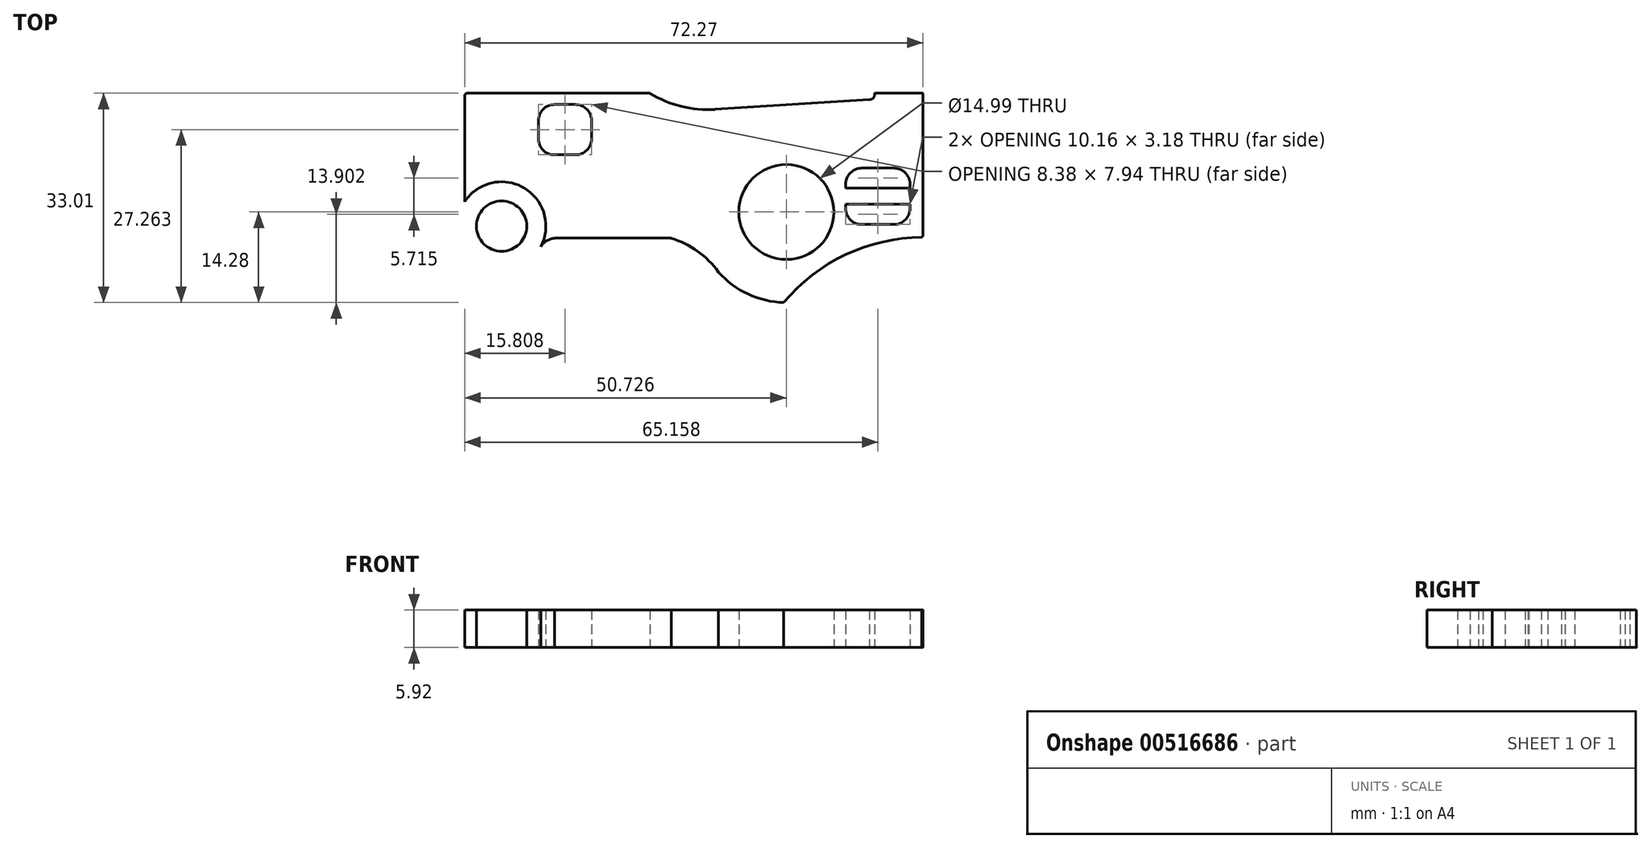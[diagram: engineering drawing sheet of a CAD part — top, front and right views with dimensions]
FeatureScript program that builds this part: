
annotation { "Feature Type Name" : "Feature", "Feature Type Description" : "" }
export const myFeature = defineFeature(function(context is Context, id is Id, definition is map)
    precondition{}
    {
        {
            var Q0;
            Q0=qCreatedBy(makeId("Top.planeOp"),FACE);
            var sketch = newSketch(context, id + "F0", { "sketchPlane" : qUnion([Q0])});
            skLineSegment(sketch, "E0.bottom", {"start": v(39.25, -10.6) * mm, "end": v(31.72, -10.6) * mm});
            skLineSegment(sketch, "E1.trimOffspring", {"start": v(-3.76, -10.6) * mm, "end": v(-32.6, -10.6) * mm});
            skLineSegment(sketch, "E2.MirrorCS", {"start": v(31.67, -10.8) * mm, "end": v(31.67, -10.64) * mm});
            skArc(sketch, "E3.MirrorCS", {"start": v(31.67, -10.8) * mm, "mid": v(31.43, -11.37) * mm, "end": v(30.86, -11.6) * mm});
            skArc(sketch, "E4.MirrorCS", {"start": v(31.67, -10.64) * mm, "mid": v(31.69, -10.6) * mm, "end": v(31.72, -10.6) * mm});
            skArc(sketch, "E5.MirrorCS", {"start": v(39.25, -10.6) * mm, "mid": v(39.29, -10.6) * mm, "end": v(39.3, -10.64) * mm});
            skLineSegment(sketch, "E6.MirrorCS", {"start": v(-29.64, -12.5) * mm, "end": v(-29.8, -12.5) * mm});
            skLineSegment(sketch, "E7.MirrorCS", {"start": v(-27.09, -21.38) * mm, "end": v(-27.1, -21.38) * mm});
            skArc(sketch, "E8.MirrorCS", {"start": v(-32.97, -10.97) * mm, "mid": v(-32.86, -10.7) * mm, "end": v(-32.6, -10.6) * mm});
            skArc(sketch, "E9.MirrorCS", {"start": v(-31.06, -13.76) * mm, "mid": v(-30.7, -12.87) * mm, "end": v(-29.8, -12.5) * mm});
            skArc(sketch, "E10.MirrorCS", {"start": v(-25.82, -13.76) * mm, "mid": v(-25.45, -12.87) * mm, "end": v(-24.55, -12.5) * mm});
            skArc(sketch, "E11.MirrorCS", {"start": v(-24.4, -12.5) * mm, "mid": v(-23.5, -12.87) * mm, "end": v(-23.13, -13.76) * mm});
            skArc(sketch, "E12.MirrorCS", {"start": v(-27.1, -21.38) * mm, "mid": v(-28, -21.01) * mm, "end": v(-28.37, -20.11) * mm});
            skArc(sketch, "E13.MirrorCS", {"start": v(-25.82, -20.11) * mm, "mid": v(-26.19, -21.01) * mm, "end": v(-27.09, -21.38) * mm});
            skArc(sketch, "E14.MirrorCS", {"start": v(-29.64, -12.5) * mm, "mid": v(-28.74, -12.87) * mm, "end": v(-28.37, -13.76) * mm});
            skLineSegment(sketch, "E15.MirrorCS", {"start": v(-24.55, -12.5) * mm, "end": v(-24.4, -12.5) * mm});
            skLineSegment(sketch, "E16.MirrorCS", {"start": v(-21.35, -25.87) * mm, "end": v(-21.35, -27.66) * mm});
            skArc(sketch, "E17.MirrorCS", {"start": v(39.3, -32.94) * mm, "mid": v(39.26, -33.15) * mm, "end": v(39.13, -33.32) * mm});
            skLineSegment(sketch, "E18.MirrorCS", {"start": v(4.8, -17.77) * mm, "end": v(4.8, -17.33) * mm});
            skLineSegment(sketch, "E19.MirrorCS", {"start": v(-1.92, -13.96) * mm, "end": v(2.73, -14.84) * mm});
            skArc(sketch, "E20.MirrorCS", {"start": v(-18.81, -20.3) * mm, "mid": v(-20.6, -19.56) * mm, "end": v(-21.35, -17.77) * mm});
            skLineSegment(sketch, "E21.MirrorCS", {"start": v(37.27, -28.75) * mm, "end": v(37.27, -24.94) * mm});
            skArc(sketch, "E22.MirrorCS", {"start": v(-21.35, -25.87) * mm, "mid": v(-20.6, -24.08) * mm, "end": v(-18.81, -23.33) * mm});
            skArc(sketch, "E23.MirrorCS", {"start": v(4.8, -17.77) * mm, "mid": v(4.06, -19.56) * mm, "end": v(2.26, -20.3) * mm});
            skArc(sketch, "E24.MirrorCS", {"start": v(-12.97, -17.77) * mm, "mid": v(-13.72, -19.56) * mm, "end": v(-15.51, -20.3) * mm});
            skArc(sketch, "E25.MirrorCS", {"start": v(29.65, -31.29) * mm, "mid": v(27.85, -30.54) * mm, "end": v(27.1, -28.75) * mm});
            skArc(sketch, "E26.MirrorCS", {"start": v(-18.81, -31.55) * mm, "mid": v(-19.53, -31.44) * mm, "end": v(-20.18, -31.15) * mm});
            skArc(sketch, "E27.MirrorCS", {"start": v(-21.35, -14.9) * mm, "mid": v(-20.6, -13.11) * mm, "end": v(-18.81, -12.37) * mm});
            skArc(sketch, "E28.MirrorCS", {"start": v(2.73, -14.84) * mm, "mid": v(4.22, -15.71) * mm, "end": v(4.8, -17.33) * mm});
            skArc(sketch, "E29.MirrorCS", {"start": v(-15.51, -12.37) * mm, "mid": v(-13.72, -13.11) * mm, "end": v(-12.97, -14.9) * mm});
            skArc(sketch, "E30.MirrorCS", {"start": v(27.1, -24.94) * mm, "mid": v(27.85, -23.14) * mm, "end": v(29.65, -22.4) * mm});
            skLineSegment(sketch, "E31.MirrorCS", {"start": v(-1.92, -20.3) * mm, "end": v(2.26, -20.3) * mm});
            skArc(sketch, "E32.MirrorCS", {"start": v(34.73, -22.4) * mm, "mid": v(36.52, -23.14) * mm, "end": v(37.27, -24.94) * mm});
            skLineSegment(sketch, "E33.MirrorCS", {"start": v(-4.46, -17.77) * mm, "end": v(-4.46, -16.5) * mm});
            skLineSegment(sketch, "E34.MirrorCS", {"start": v(-21.35, -17.77) * mm, "end": v(-21.35, -14.9) * mm});
            skLineSegment(sketch, "E35.MirrorCS", {"start": v(6.1, -13.27) * mm, "end": v(6.1, -20.26) * mm});
            skArc(sketch, "E36.MirrorCS", {"start": v(-1.92, -20.3) * mm, "mid": v(-3.72, -19.56) * mm, "end": v(-4.46, -17.77) * mm});
            skLineSegment(sketch, "E37.MirrorCS", {"start": v(-12.97, -17.77) * mm, "end": v(-12.97, -14.9) * mm});
            skArc(sketch, "E38.MirrorCS", {"start": v(37.27, -28.75) * mm, "mid": v(36.52, -30.54) * mm, "end": v(34.73, -31.29) * mm});
            skLineSegment(sketch, "E39.MirrorCS", {"start": v(4.73, -30.07) * mm, "end": v(6.18, -26.94) * mm});
            skArc(sketch, "E40.MirrorCS", {"start": v(-4.46, -16.5) * mm, "mid": v(-3.72, -14.7) * mm, "end": v(-1.92, -13.96) * mm});
            skLineSegment(sketch, "E41.MirrorCS", {"start": v(-18.81, -20.3) * mm, "end": v(-15.51, -20.3) * mm});
            skLineSegment(sketch, "E42.MirrorCS", {"start": v(-18.81, -12.37) * mm, "end": v(-15.51, -12.37) * mm});
            skLineSegment(sketch, "E43.MirrorCS", {"start": v(27.1, -28.75) * mm, "end": v(27.1, -24.94) * mm});
            skArc(sketch, "E44.MirrorCS", {"start": v(4.73, -30.07) * mm, "mid": v(3.8, -31.15) * mm, "end": v(2.43, -31.55) * mm});
            skArc(sketch, "E45.MirrorCS", {"start": v(-21.07, -34.98) * mm, "mid": v(-20.15, -33.92) * mm, "end": v(-18.83, -33.45) * mm});
            skPoint(sketch, "E46.MirrorP", {"position": v(2.6, -27.6) * mm});
            skLineSegment(sketch, "E47.MirrorCS", {"start": v(-23.13, -25.84) * mm, "end": v(-23.13, -13.76) * mm});
            skLineSegment(sketch, "E48.MirrorCS", {"start": v(-31.06, -13.76) * mm, "end": v(-31.06, -25.76) * mm});
            skCircle(sketch, "E49.MirrorC", {"center": v(17.76, -29.32) * mm, "radius": 7.5 * mm});
            skLineSegment(sketch, "E50.MirrorCS", {"start": v(-25.82, -20.11) * mm, "end": v(-25.82, -13.76) * mm});
            skLineSegment(sketch, "E51.MirrorCS", {"start": v(-32.97, -10.97) * mm, "end": v(-32.97, -27.68) * mm});
            skArc(sketch, "E52.MirrorCS", {"start": v(17.35, -43.6) * mm, "mid": v(11.71, -42.27) * mm, "end": v(7.07, -38.8) * mm});
            skLineSegment(sketch, "E53.MirrorCS", {"start": v(-18.81, -31.55) * mm, "end": v(2.43, -31.55) * mm});
            skLineSegment(sketch, "E54.MirrorCS", {"start": v(-28.37, -20.11) * mm, "end": v(-28.37, -13.76) * mm});
            skArc(sketch, "E55.MirrorCS", {"start": v(17.35, -43.6) * mm, "mid": v(27.1, -36.05) * mm, "end": v(39.13, -33.32) * mm});
            skLineSegment(sketch, "E56.MirrorCS", {"start": v(-0.42, -33.45) * mm, "end": v(-18.83, -33.45) * mm});
            skLineSegment(sketch, "E57.MirrorCS", {"start": v(-18.81, -23.33) * mm, "end": v(3.88, -23.33) * mm});
            skLineSegment(sketch, "E58.MirrorCS", {"start": v(30.88, -11.73) * mm, "end": v(30.88, -18.71) * mm});
            skLineSegment(sketch, "E59.MirrorCS", {"start": v(6.1, -20.26) * mm, "end": v(30.88, -18.71) * mm});
            skLineSegment(sketch, "E60.MirrorCS", {"start": v(39.3, -32.94) * mm, "end": v(39.3, -10.64) * mm});
            skLineSegment(sketch, "E61.MirrorCS", {"start": v(30.86, -11.6) * mm, "end": v(6.53, -13.13) * mm});
            skArc(sketch, "E62.MirrorCS", {"start": v(6.53, -13.13) * mm, "mid": v(1.19, -12.65) * mm, "end": v(-3.76, -10.6) * mm});
            skCircle(sketch, "E63.MirrorC", {"center": v(17.76, -29.32) * mm, "radius": 6.03 * mm});
            skLineSegment(sketch, "E64.MirrorCS", {"start": v(6.1, -13.27) * mm, "end": v(30.88, -11.73) * mm});
            skLineSegment(sketch, "E65.MirrorCS", {"start": v(34.73, -31.29) * mm, "end": v(29.65, -31.29) * mm});
            skArc(sketch, "E66.MirrorCS", {"start": v(-0.42, -33.45) * mm, "mid": v(3.77, -35.52) * mm, "end": v(7.07, -38.8) * mm});
            skLineSegment(sketch, "E67.MirrorCS", {"start": v(27.1, -28.11) * mm, "end": v(37.27, -28.11) * mm});
            skArc(sketch, "E68.MirrorCS", {"start": v(-31.06, -25.76) * mm, "mid": v(-27.08, -24.56) * mm, "end": v(-23.13, -25.84) * mm});
            skLineSegment(sketch, "E69.MirrorCS", {"start": v(34.73, -22.4) * mm, "end": v(29.65, -22.4) * mm});
            skCircle(sketch, "E70.MirrorC", {"center": v(-27.15, -31.55) * mm, "radius": 3.97 * mm});
            skArc(sketch, "E71.MirrorCS", {"start": v(3.88, -23.33) * mm, "mid": v(6.02, -24.5) * mm, "end": v(6.18, -26.94) * mm});
            skLineSegment(sketch, "E72.MirrorCS", {"start": v(27.1, -25.57) * mm, "end": v(37.27, -25.57) * mm});
            skCircle(sketch, "E73.MirrorC", {"center": v(-27.15, -31.55) * mm, "radius": 6.99 * mm});
            skSolve(sketch);
        }
        {
            var Q0;
            Q0=makeQuery(id+"F0.imprint","IMPRINT",FACE,{"disambiguationData":[TD([[makeQuery(id+"F0.imprint","IMPRINT",EDGE,{"derivedFrom":sQuery(id+"F0.wireOp",EDGE,"E70.MirrorC")}),1.0]])]});
            var Q1;
            {var subQ2=sQuery(id+"F0.wireOp",EDGE,"E16.MirrorCS");Q1=makeQuery(id+"F0.imprint","IMPRINT",FACE,{"disambiguationData":[TD([[makeQuery(id+"F0.imprint","IMPRINT",EDGE,{"derivedFrom":subQ2}),1.0]])]});}
            var Q2;
            {var subQ4=sQuery(id+"F0.wireOp",EDGE,"E30.MirrorCS");Q2=makeQuery(id+"F0.imprint","IMPRINT",FACE,{"disambiguationData":[TD([[makeQuery(id+"F0.imprint","IMPRINT",EDGE,{"derivedFrom":subQ4}),-1.0]])]});}
            var Q3;
            {var subQ1=sQuery(id+"F0.wireOp",EDGE,"E25.MirrorCS");Q3=makeQuery(id+"F0.imprint","IMPRINT",FACE,{"disambiguationData":[TD([[makeQuery(id+"F0.imprint","IMPRINT",EDGE,{"derivedFrom":subQ1}),-1.0]])]});}
            var Q4;
            Q4=makeQuery(id+"F0.imprint","IMPRINT",FACE,{"disambiguationData":[TD([[makeQuery(id+"F0.imprint","IMPRINT",EDGE,{"derivedFrom":sQuery(id+"F0.wireOp",EDGE,"E35.MirrorCS")}),1.0]])]});
            var Q5;
            {var subQ0=sQuery(id+"F0.wireOp",EDGE,"E67.MirrorCS");Q5=makeQuery(id+"F0.imprint","IMPRINT",FACE,{"disambiguationData":[TD([[makeQuery(id+"F0.imprint","IMPRINT",EDGE,{"derivedFrom":subQ0}),1.0]])]});}
            var Q6;
            Q6=makeQuery(id+"F0.imprint","IMPRINT",FACE,{"disambiguationData":[TD([[makeQuery(id+"F0.imprint","IMPRINT",EDGE,{"derivedFrom":sQuery(id+"F0.wireOp",EDGE,"E6.MirrorCS")}),1.0]])]});
            var Q7;
            Q7=makeQuery(id+"F0.imprint","IMPRINT",FACE,{"disambiguationData":[TD([[makeQuery(id+"F0.imprint","IMPRINT",EDGE,{"derivedFrom":sQuery(id+"F0.wireOp",EDGE,"E1.trimOffspring")}),1.0]])]});
            var Q8;
            Q8=makeQuery(id+"F0.imprint","IMPRINT",FACE,{"disambiguationData":[TD([[makeQuery(id+"F0.imprint","IMPRINT",EDGE,{"derivedFrom":sQuery(id+"F0.wireOp",EDGE,"E20.MirrorCS")}),-1.0]])]});
            var Q9;
            Q9=makeQuery(id+"F0.imprint","IMPRINT",FACE,{"disambiguationData":[TD([[makeQuery(id+"F0.imprint","IMPRINT",EDGE,{"derivedFrom":sQuery(id+"F0.wireOp",EDGE,"E18.MirrorCS")}),1.0]])]});
            var Q10;
            Q10=makeQuery(id+"F0.imprint","IMPRINT",FACE,{"disambiguationData":[TD([[makeQuery(id+"F0.imprint","IMPRINT",EDGE,{"derivedFrom":sQuery(id+"F0.wireOp",EDGE,"E49.MirrorC")}),-1.0]])]});
            extrude(context, id + "F1", {"entities" : qUnion([Q0, Q1, Q2, Q3, Q4, Q5, Q6, Q7, Q8, Q9, Q10]), "depth" : 5.92 * mm, "offsetDistance" : 25.4 * mm});
        }
    });
